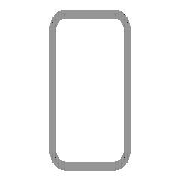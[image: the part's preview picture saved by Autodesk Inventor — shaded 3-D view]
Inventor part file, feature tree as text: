
AUTODESK INVENTOR PART (.ipt)
format: ipt  version: 2025 (Build 290162010, 162A)  size: 142,848 bytes
history: native  units: mm (DEFAULTED — no unit token found)
features: other x4, sketch x1, plane x1
ambient origin geometry x8: Origin, YZ Plane, XZ Plane, XY Plane, X Axis, Y Axis, Z Axis, Center Point
bodies: Solid1 (feature_tree), Body (feature_tree)
feature tree (6):
  parser-record x1  (decoder bookkeeping rows leaked as tree rows — omitted from the tree; the rows remain in map.json)
  other  "Driven Length"
  other  "Start Plane"
  other  "End Plane"
  sketch  "Sketch3"  dims[d3=720.0mm d4=0.0mm d7=6.0mm d9=40.0mm d11=60.0mm d12=3.0mm d13=40.0mm d14=760.0mm d15=20.0mm d16=30.0mm d17=90.0deg d18=720.0mm]
  plane  "Work Plane3"
